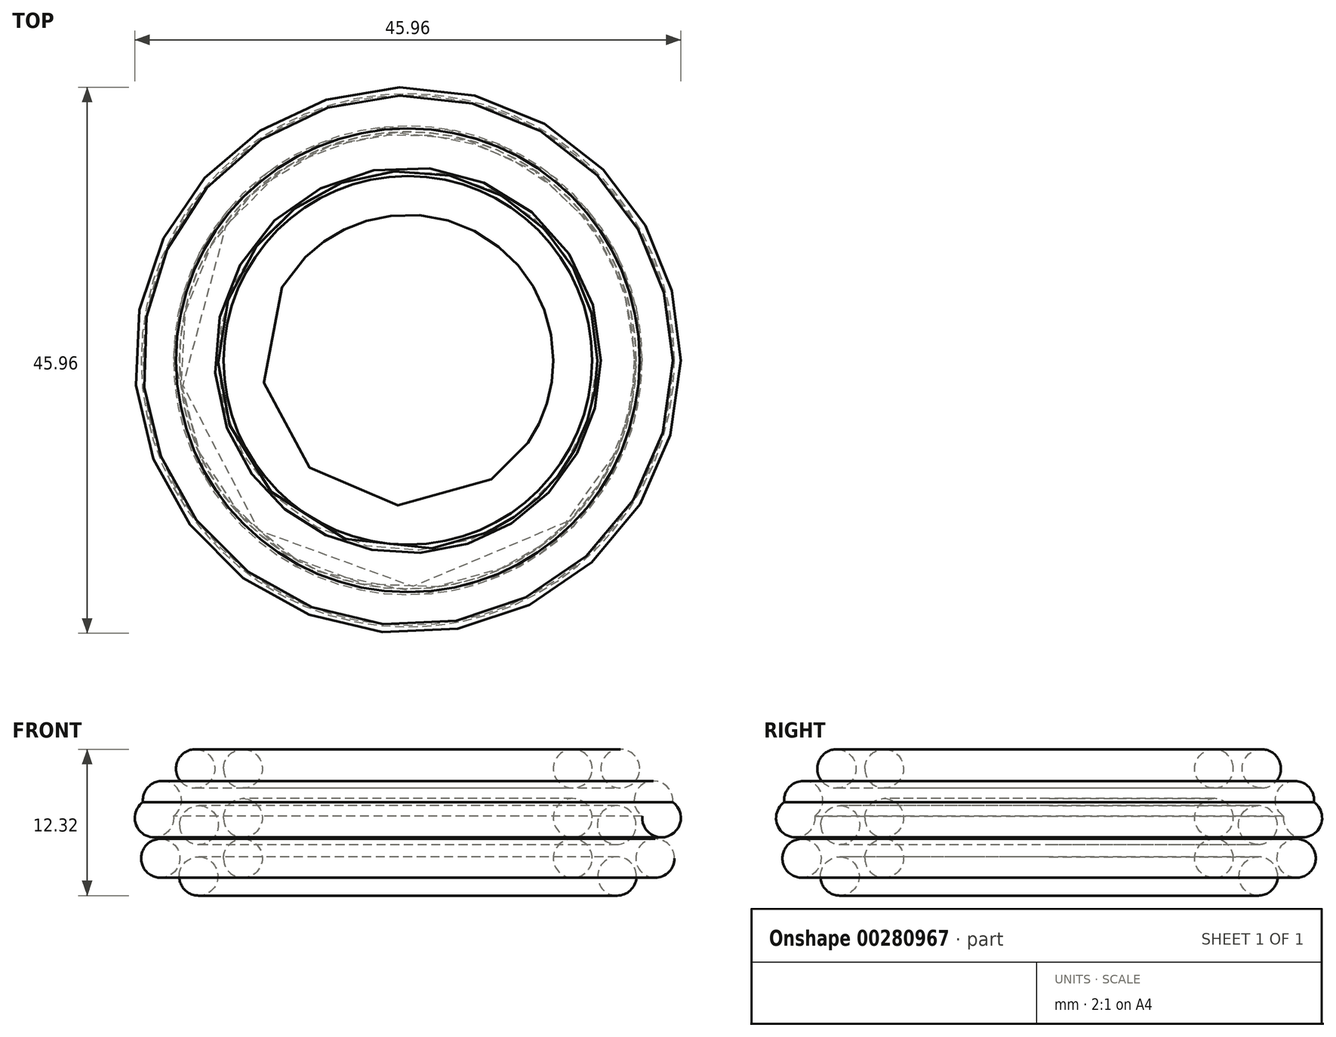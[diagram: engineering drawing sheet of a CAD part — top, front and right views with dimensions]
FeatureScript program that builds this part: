
annotation { "Feature Type Name" : "Feature", "Feature Type Description" : "" }
export const myFeature = defineFeature(function(context is Context, id is Id, definition is map)
    precondition{}
    {
        {
            var Q0;
            Q0=qCreatedBy(makeId("Front.planeOp"),FACE);
            var sketch = newSketch(context, id + "F0", { "sketchPlane" : qUnion([Q0])});
            skCircle(sketch, "E0", {"center": v(-17.57, 14.47) * mm, "radius": 1.63 * mm});
            skCircle(sketch, "E1", {"center": v(-17.88, 19.22) * mm, "radius": 1.63 * mm});
            skCircle(sketch, "E2", {"center": v(-21.34, 15.07) * mm, "radius": 1.63 * mm});
            skCircle(sketch, "E3", {"center": v(-17.6, 10.16) * mm, "radius": 1.63 * mm});
            skCircle(sketch, "E4", {"center": v(-20.67, 16.55) * mm, "radius": 1.63 * mm});
            skCircle(sketch, "E5", {"center": v(-13.87, 11.67) * mm, "radius": 1.63 * mm});
            skCircle(sketch, "E6", {"center": v(-20.81, 11.67) * mm, "radius": 1.63 * mm});
            skCircle(sketch, "E7", {"center": v(-13.87, 15.07) * mm, "radius": 1.63 * mm});
            skCircle(sketch, "E8", {"center": v(-13.87, 19.22) * mm, "radius": 1.63 * mm});
            skLineSegment(sketch, "E9", {"start": v(0, 32.42) * mm, "end": v(0, 0) * mm, "construction": true});
            skSolve(sketch);
        }
        {
            var Q0;
            Q0=makeQuery(id+"F0.imprint","IMPRINT",FACE,{"disambiguationData":[TD([[makeQuery(id+"F0.imprint","IMPRINT",EDGE,{"derivedFrom":sQuery(id+"F0.wireOp",EDGE,"E3")}),1.0]])]});
            var Q1;
            {var subQ0=sQuery(id+"F0.wireOp",EDGE,"E4");var subQ1=sQuery(id+"F0.wireOp",EDGE,"E2");var subQ2=makeQuery(id+"F0.imprint","INTERSECT",VERTEX,{"disambiguationData":[OD(0.0)],"derivedFrom":[subQ1,subQ0]});Q1=makeQuery(id+"F0.imprint","IMPRINT",FACE,{"disambiguationData":[TD([[makeQuery(id+"F0.imprint","IMPRINT",EDGE,{"disambiguationData":[TD([[subQ2,1.0]])],"derivedFrom":subQ1}),1.0]])]});}
            var Q2;
            {var subQ0=sQuery(id+"F0.wireOp",EDGE,"E4");var subQ1=sQuery(id+"F0.wireOp",EDGE,"E2");var subQ2=makeQuery(id+"F0.imprint","INTERSECT",VERTEX,{"disambiguationData":[OD(0.0)],"derivedFrom":[subQ1,subQ0]});Q2=makeQuery(id+"F0.imprint","IMPRINT",FACE,{"disambiguationData":[TD([[makeQuery(id+"F0.imprint","IMPRINT",EDGE,{"disambiguationData":[TD([[subQ2,-1.0]])],"derivedFrom":subQ1}),1.0]])]});}
            var Q3;
            {var subQ0=sQuery(id+"F0.wireOp",EDGE,"E4");var subQ1=sQuery(id+"F0.wireOp",EDGE,"E2");var subQ2=makeQuery(id+"F0.imprint","INTERSECT",VERTEX,{"disambiguationData":[OD(0.0)],"derivedFrom":[subQ1,subQ0]});Q3=makeQuery(id+"F0.imprint","IMPRINT",FACE,{"disambiguationData":[TD([[makeQuery(id+"F0.imprint","IMPRINT",EDGE,{"disambiguationData":[TD([[subQ2,1.0]])],"derivedFrom":subQ1}),-1.0]])]});}
            var Q4;
            Q4=makeQuery(id+"F0.imprint","IMPRINT",FACE,{"disambiguationData":[TD([[makeQuery(id+"F0.imprint","IMPRINT",EDGE,{"derivedFrom":sQuery(id+"F0.wireOp",EDGE,"E1")}),1.0]])]});
            var Q5;
            Q5=makeQuery(id+"F0.imprint","IMPRINT",FACE,{"disambiguationData":[TD([[makeQuery(id+"F0.imprint","IMPRINT",EDGE,{"derivedFrom":sQuery(id+"F0.wireOp",EDGE,"E0")}),1.0]])]});
            var Q6;
            Q6=makeQuery(id+"F0.imprint","IMPRINT",FACE,{"disambiguationData":[TD([[makeQuery(id+"F0.imprint","IMPRINT",EDGE,{"derivedFrom":sQuery(id+"F0.wireOp",EDGE,"E8")}),1.0]])]});
            var Q7;
            Q7=makeQuery(id+"F0.imprint","IMPRINT",FACE,{"disambiguationData":[TD([[makeQuery(id+"F0.imprint","IMPRINT",EDGE,{"derivedFrom":sQuery(id+"F0.wireOp",EDGE,"E7")}),1.0]])]});
            var Q8;
            Q8=makeQuery(id+"F0.imprint","IMPRINT",FACE,{"disambiguationData":[TD([[makeQuery(id+"F0.imprint","IMPRINT",EDGE,{"derivedFrom":sQuery(id+"F0.wireOp",EDGE,"E5")}),1.0]])]});
            var Q9;
            Q9=makeQuery(id+"F0.imprint","IMPRINT",FACE,{"disambiguationData":[TD([[makeQuery(id+"F0.imprint","IMPRINT",EDGE,{"derivedFrom":sQuery(id+"F0.wireOp",EDGE,"E6")}),1.0]])]});
            var Q10;
            Q10=sQuery(id+"F0.wireOp",EDGE,"E9");
            revolve(context, id + "F1", {"entities" : qUnion([Q0, Q1, Q2, Q3, Q4, Q5, Q6, Q7, Q8, Q9]), "axis" : qUnion([Q10]), "revolveType" : RevolveType.FULL});
        }
    });
